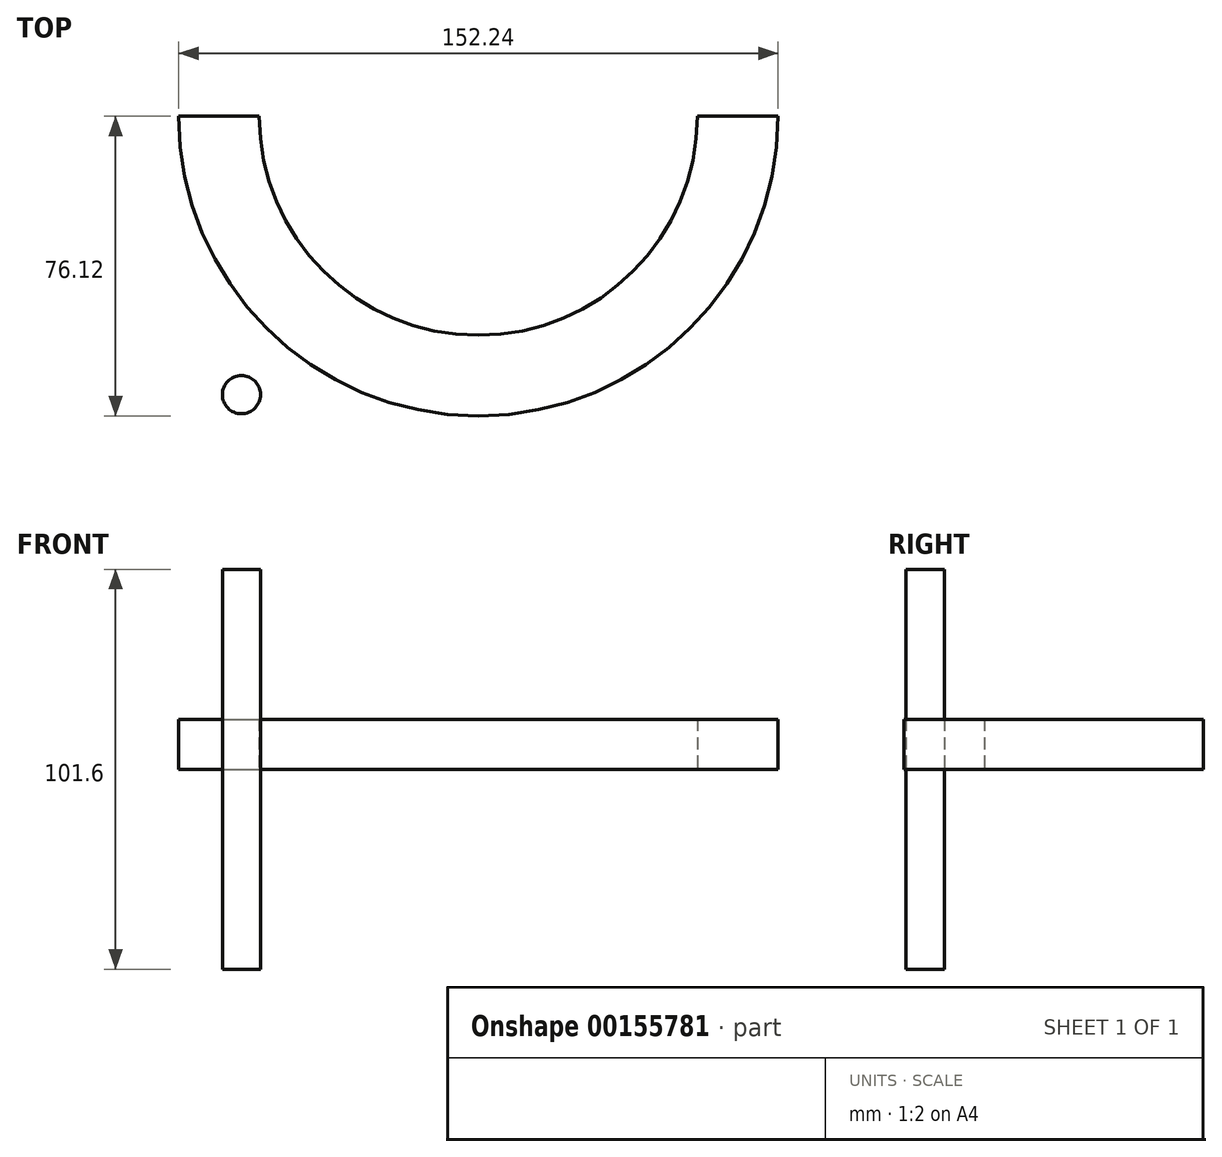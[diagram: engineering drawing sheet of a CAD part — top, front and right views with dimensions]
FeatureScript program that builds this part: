
annotation { "Feature Type Name" : "Feature", "Feature Type Description" : "" }
export const myFeature = defineFeature(function(context is Context, id is Id, definition is map)
    precondition{}
    {
        {
            var Q0;
            Q0=qCreatedBy(makeId("Top.planeOp"),FACE);
            var sketch = newSketch(context, id + "F0", { "sketchPlane" : qUnion([Q0])});
            skArc(sketch, "E0", {"start": v(-76.12, 0) * mm, "mid": v(0, -76.12) * mm, "end": v(76.12, 0) * mm});
            skArc(sketch, "E1", {"start": v(-55.65, 0) * mm, "mid": v(0, -55.65) * mm, "end": v(55.65, 0) * mm});
            skLineSegment(sketch, "E2", {"start": v(-76.12, 0) * mm, "end": v(-55.65, 0) * mm});
            skLineSegment(sketch, "E3", {"start": v(55.65, 0) * mm, "end": v(76.12, 0) * mm});
            skSolve(sketch);
        }
        {
            var Q0;
            Q0=makeQuery(id+"F0.imprint","IMPRINT",FACE,{"disambiguationData":[TD([[makeQuery(id+"F0.imprint","IMPRINT",EDGE,{"derivedFrom":sQuery(id+"F0.wireOp",EDGE,"E0")}),1.0]])]});
            extrude(context, id + "F1", {"entities" : qUnion([Q0]), "depth" : 12.7 * mm});
        }
        {
            var Q0;
            Q0=qCreatedBy(makeId("Top.planeOp"),FACE);
            var sketch = newSketch(context, id + "F2", { "sketchPlane" : qUnion([Q0])});
            skCircle(sketch, "E4", {"center": v(-60.18, -70.72) * mm, "radius": 4.84 * mm});
            skSolve(sketch);
        }
        {
            var Q0;
            Q0=makeQuery(id+"F2.imprint","IMPRINT",FACE,{"disambiguationData":[TD([[makeQuery(id+"F2.imprint","IMPRINT",EDGE,{"derivedFrom":sQuery(id+"F2.wireOp",EDGE,"E4")}),1.0]])]});
            extrude(context, id + "F3", {"entities" : qUnion([Q0]), "endBound" : BoundingType.SYMMETRIC, "depth" : 101.6 * mm});
        }
    });
